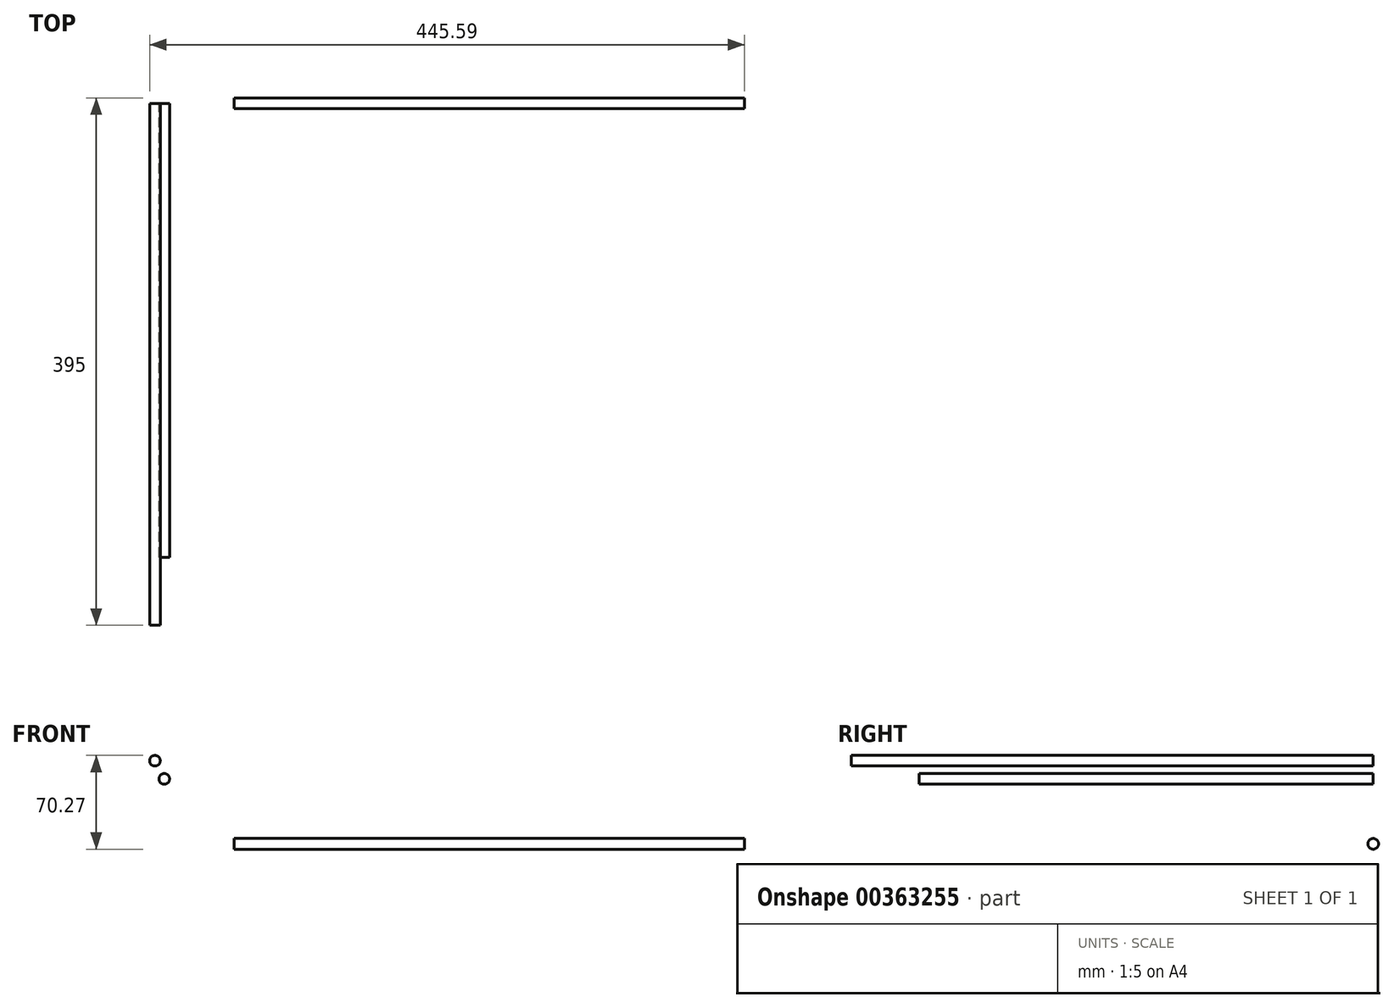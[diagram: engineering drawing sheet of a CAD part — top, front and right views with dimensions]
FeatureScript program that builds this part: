
annotation { "Feature Type Name" : "Feature", "Feature Type Description" : "" }
export const myFeature = defineFeature(function(context is Context, id is Id, definition is map)
    precondition{}
    {
        {
            var Q0;
            Q0=qCreatedBy(makeId("Right.planeOp"),FACE);
            var sketch = newSketch(context, id + "F0", { "sketchPlane" : qUnion([Q0])});
            skCircle(sketch, "E0", {"center": v(0, 0) * mm, "radius": 4 * mm});
            skSolve(sketch);
        }
        {
            var Q0;
            Q0=qCreatedBy(makeId("Front.planeOp"),FACE);
            var sketch = newSketch(context, id + "F1", { "sketchPlane" : qUnion([Q0])});
            skCircle(sketch, "E1", {"center": v(-59.4, 62.27) * mm, "radius": 4 * mm});
            skSolve(sketch);
        }
        {
            assignVariable(context, id + "F2", {"name" : "X", "anyValue" : 295});
        }
        {
            assignVariable(context, id + "F3", {"name" : "Y", "anyValue" : 308});
        }
        {
            var Q0;
            Q0=makeQuery(id+"F0.imprint","IMPRINT",FACE,{"disambiguationData":[TD([[makeQuery(id+"F0.imprint","IMPRINT",EDGE,{"derivedFrom":sQuery(id+"F0.wireOp",EDGE,"E0")}),1.0]])]});
            var Q1;
            Q1=sQuery(id+"F0.wireOp",EDGE,"E0");
            extrude(context, id + "F4", {"entities" : qUnion([Q0]), "surfaceEntities" : qUnion([Q1]), "depth" : (getVariable(context, 'X') + 87.17) * mm});
        }
        {
            var Q0;
            Q0=makeQuery(id+"F1.imprint","IMPRINT",FACE,{"disambiguationData":[TD([[makeQuery(id+"F1.imprint","IMPRINT",EDGE,{"derivedFrom":sQuery(id+"F1.wireOp",EDGE,"E1")}),1.0]])]});
            var Q1;
            Q1=sQuery(id+"F1.wireOp",EDGE,"E1");
            extrude(context, id + "F5", {"entities" : qUnion([Q0]), "surfaceEntities" : qUnion([Q1]), "depth" : (getVariable(context, 'Y') + 83) * mm});
        }
        {
            var Q0;
            Q0=qCreatedBy(makeId("Front.planeOp"),FACE);
            var sketch = newSketch(context, id + "F6", { "sketchPlane" : qUnion([Q0])});
            skCircle(sketch, "E2", {"center": v(-52.4, 48.69) * mm, "radius": 4 * mm});
            skSolve(sketch);
        }
        {
            var Q0;
            Q0=makeQuery(id+"F6.imprint","IMPRINT",FACE,{"disambiguationData":[TD([[makeQuery(id+"F6.imprint","IMPRINT",EDGE,{"derivedFrom":sQuery(id+"F6.wireOp",EDGE,"E2")}),1.0]])]});
            extrude(context, id + "F7", {"entities" : qUnion([Q0]), "depth" : 340 * mm});
        }
    });
